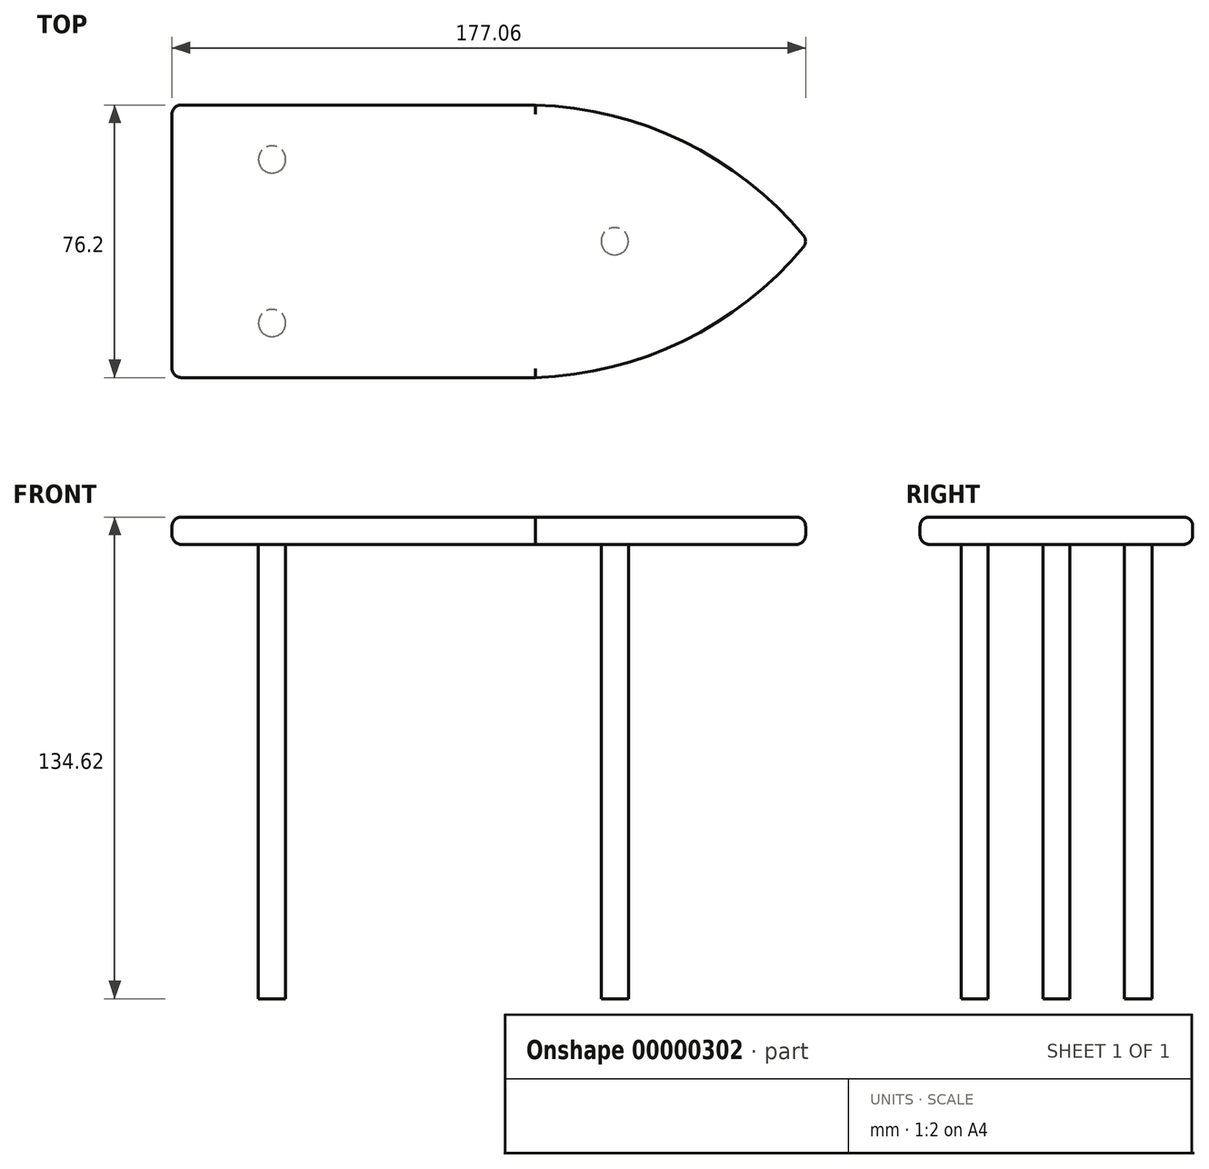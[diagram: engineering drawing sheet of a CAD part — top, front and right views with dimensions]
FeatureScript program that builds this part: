
annotation { "Feature Type Name" : "Feature", "Feature Type Description" : "" }
export const myFeature = defineFeature(function(context is Context, id is Id, definition is map)
    precondition{}
    {
        {
            var Q0;
            Q0=qCreatedBy(makeId("Top.planeOp"),FACE);
            var sketch = newSketch(context, id + "F0", { "sketchPlane" : qUnion([Q0])});
            skLineSegment(sketch, "E0.bottom", {"start": v(0, 0) * mm, "end": v(177.8, 0) * mm});
            skLineSegment(sketch, "E0.top", {"start": v(0, 76.2) * mm, "end": v(177.8, 76.2) * mm});
            skLineSegment(sketch, "E0.left", {"start": v(0, 0) * mm, "end": v(0, 76.2) * mm});
            skLineSegment(sketch, "E0.right", {"start": v(177.8, 0) * mm, "end": v(177.8, 76.2) * mm});
            skPoint(sketch, "E1", {"position": v(177.8, 38.1) * mm});
            skArc(sketch, "E2", {"start": v(101.6, 0) * mm, "mid": v(143.89, 10.68) * mm, "end": v(177.8, 38.1) * mm});
            skPoint(sketch, "E3", {"position": v(101.6, 76.2) * mm});
            skArc(sketch, "E4", {"start": v(177.8, 38.1) * mm, "mid": v(143.89, 65.52) * mm, "end": v(101.6, 76.2) * mm});
            skLineSegment(sketch, "E5", {"start": v(147.15, 123.6) * mm, "end": v(147.15, -54.73) * mm});
            skSolve(sketch);
        }
        {
            var Q0;
            {var subQ7=sQuery(id+"F0.wireOp",EDGE,"E0.left");Q0=makeQuery(id+"F0.imprint","IMPRINT",FACE,{"disambiguationData":[TD([[makeQuery(id+"F0.imprint","IMPRINT",EDGE,{"derivedFrom":subQ7}),-1.0]])]});}
            var Q1;
            {var subQ0=sQuery(id+"F0.wireOp",EDGE,"E5");var subQ3=sQuery(id+"F0.wireOp",EDGE,"E2");var subQ4=makeQuery(id+"F0.imprint","INTERSECT",VERTEX,{"derivedFrom":[subQ3,subQ0]});Q1=makeQuery(id+"F0.imprint","IMPRINT",FACE,{"disambiguationData":[TD([[makeQuery(id+"F0.imprint","IMPRINT",EDGE,{"disambiguationData":[TD([[subQ4,1.0]])],"derivedFrom":subQ0}),1.0]])]});}
            extrude(context, id + "F1", {"entities" : qUnion([Q0, Q1]), "depth" : 7.62 * mm});
        }
        {
            var Q0;
            Q0=makeQuery(id+"F1.opExtrude","CAP_FACE",FACE,{"disambiguationData":[OSD([sQuery(id+"F0.wireOp",EDGE,"E0.bottom"),sQuery(id+"F0.wireOp",EDGE,"E0.top"),sQuery(id+"F0.wireOp",EDGE,"E0.left"),sQuery(id+"F0.wireOp",EDGE,"E2"),sQuery(id+"F0.wireOp",EDGE,"E4")])],"isStart":true});
            var Q1;
            Q1=makeQuery(id+"F1.opExtrude","CAP_FACE",FACE,{"disambiguationData":[OSD([sQuery(id+"F0.wireOp",EDGE,"E0.bottom"),sQuery(id+"F0.wireOp",EDGE,"E0.top"),sQuery(id+"F0.wireOp",EDGE,"E0.left"),sQuery(id+"F0.wireOp",EDGE,"E2"),sQuery(id+"F0.wireOp",EDGE,"E4")])],"isStart":false});
            var Q2;
            Q2=makeQuery(id+"F1.opExtrude","SWEPT_EDGE",EDGE,{"disambiguationData":[OSD([sQuery(id+"F0.wireOp",EDGE,"E0.right"),sQuery(id+"F0.wireOp",EDGE,"E2"),sQuery(id+"F0.wireOp",EDGE,"E4")])]});
            fillet(context, id + "F2", {"entities" : qUnion([Q0, Q1, Q2]), "radius" : 2.54 * mm, "tangentPropagation" : true, "allowEdgeOverflow" : false});
        }
        {
            var Q0;
            Q0=makeQuery(id+"F2.opFillet","BLEND_EDGE",EDGE,{"blendedFrom":[makeQuery(id+"F1.opExtrude","CAP_EDGE",EDGE,{"disambiguationData":[OSD([sQuery(id+"F0.wireOp",EDGE,"E0.bottom")])],"isStart":false}),makeQuery(id+"F1.opExtrude","CAP_EDGE",EDGE,{"disambiguationData":[OSD([sQuery(id+"F0.wireOp",EDGE,"E0.left")])],"isStart":false})],"blendedInto":[]});
            var Q1;
            Q1=makeQuery(id+"F1.opExtrude","SWEPT_EDGE",EDGE,{"disambiguationData":[OSD([sQuery(id+"F0.wireOp",EDGE,"E0.bottom"),sQuery(id+"F0.wireOp",EDGE,"E0.left")])]});
            var Q2;
            Q2=makeQuery(id+"F2.opFillet","BLEND_EDGE",EDGE,{"blendedFrom":[makeQuery(id+"F1.opExtrude","CAP_EDGE",EDGE,{"disambiguationData":[OSD([sQuery(id+"F0.wireOp",EDGE,"E0.top")])],"isStart":false}),makeQuery(id+"F1.opExtrude","CAP_EDGE",EDGE,{"disambiguationData":[OSD([sQuery(id+"F0.wireOp",EDGE,"E0.left")])],"isStart":false})],"blendedInto":[]});
            var Q3;
            Q3=makeQuery(id+"F1.opExtrude","SWEPT_EDGE",EDGE,{"disambiguationData":[OSD([sQuery(id+"F0.wireOp",EDGE,"E0.top"),sQuery(id+"F0.wireOp",EDGE,"E0.left")])]});
            var Q4;
            Q4=makeQuery(id+"F2.opFillet","BLEND_EDGE",EDGE,{"blendedFrom":[makeQuery(id+"F1.opExtrude","CAP_EDGE",EDGE,{"disambiguationData":[OSD([sQuery(id+"F0.wireOp",EDGE,"E0.top")])],"isStart":true}),makeQuery(id+"F1.opExtrude","CAP_EDGE",EDGE,{"disambiguationData":[OSD([sQuery(id+"F0.wireOp",EDGE,"E0.left")])],"isStart":true})],"blendedInto":[]});
            fillet(context, id + "F3", {"entities" : qUnion([Q0, Q1, Q2, Q3, Q4]), "radius" : 2.54 * mm, "tangentPropagation" : true, "allowEdgeOverflow" : false});
        }
        {
            var Q0;
            Q0=makeQuery(id+"F1.opExtrude","CAP_FACE",FACE,{"disambiguationData":[OSD([sQuery(id+"F0.wireOp",EDGE,"E0.bottom"),sQuery(id+"F0.wireOp",EDGE,"E0.top"),sQuery(id+"F0.wireOp",EDGE,"E0.left"),sQuery(id+"F0.wireOp",EDGE,"E2"),sQuery(id+"F0.wireOp",EDGE,"E4")])],"isStart":true});
            var sketch = newSketch(context, id + "F4", { "sketchPlane" : qUnion([Q0])});
            skCircle(sketch, "E6", {"center": v(27.94, -15.24) * mm, "radius": 3.81 * mm});
            skCircle(sketch, "E7", {"center": v(27.94, -60.96) * mm, "radius": 3.81 * mm});
            skCircle(sketch, "E8", {"center": v(123.72, -38.1) * mm, "radius": 3.81 * mm});
            skLineSegment(sketch, "E9", {"start": v(174.52, -38.1) * mm, "end": v(123.72, -38.1) * mm});
            skSolve(sketch);
        }
        {
            var Q0;
            {var subQ1=sQuery(id+"F4.wireOp",EDGE,"E8");Q0=qUnion([makeQuery(id+"F4.imprint","IMPRINT",FACE,{"disambiguationData":[TD([[makeQuery(id+"F4.imprint","IMPRINT",EDGE,{"derivedFrom":sQuery(id+"F4.wireOp",EDGE,"E6")}),1.0]])]}),makeQuery(id+"F4.imprint","IMPRINT",FACE,{"disambiguationData":[TD([[makeQuery(id+"F4.imprint","IMPRINT",EDGE,{"derivedFrom":sQuery(id+"F4.wireOp",EDGE,"E7")}),1.0]])]}),makeQuery(id+"F4.imprint","IMPRINT",FACE,{"disambiguationData":[TD([[makeQuery(id+"F4.imprint","IMPRINT",EDGE,{"derivedFrom":subQ1}),1.0]])]})]);}
            extrude(context, id + "F5", {"entities" : qUnion([Q0]), "operationType" : NewBodyOperationType.ADD, "depth" : 127 * mm});
        }
    });
